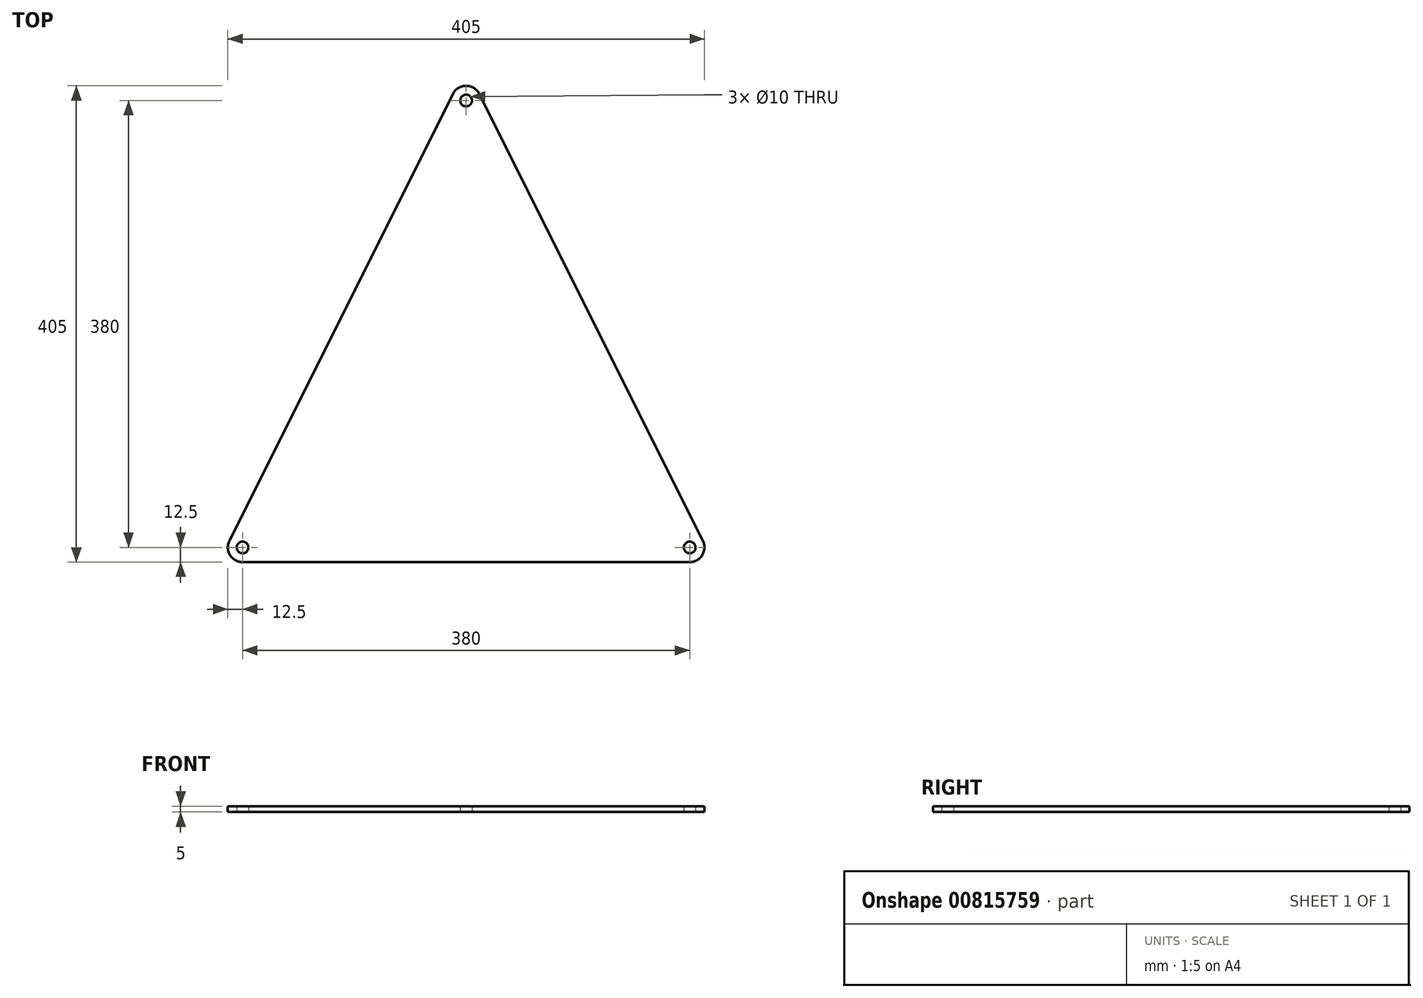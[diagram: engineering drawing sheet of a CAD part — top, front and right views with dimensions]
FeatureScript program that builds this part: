
annotation { "Feature Type Name" : "Feature", "Feature Type Description" : "" }
export const myFeature = defineFeature(function(context is Context, id is Id, definition is map)
    precondition{}
    {
        {
            var Q0;
            Q0=qCreatedBy(makeId("Top.planeOp"),FACE);
            var sketch = newSketch(context, id + "F0", { "sketchPlane" : qUnion([Q0])});
            skPoint(sketch, "E0", {"position": v(0, 190) * mm});
            skCircle(sketch, "E1", {"center": v(0, 190) * mm, "radius": 12.5 * mm});
            skPoint(sketch, "E2", {"position": v(0, -190) * mm});
            skLineSegment(sketch, "E3.top", {"start": v(190, -190) * mm, "end": v(-190, -190) * mm});
            skLineSegment(sketch, "E3.left", {"start": v(190, -190) * mm, "end": v(190, -190) * mm});
            skLineSegment(sketch, "E3.right", {"start": v(-190, -190) * mm, "end": v(-190, -190) * mm});
            skCircle(sketch, "E4", {"center": v(-190, -190) * mm, "radius": 12.5 * mm});
            skCircle(sketch, "E5", {"center": v(190, -190) * mm, "radius": 12.5 * mm});
            skLineSegment(sketch, "E6", {"start": v(0, 190) * mm, "end": v(190, -190) * mm});
            skLineSegment(sketch, "E7", {"start": v(0, 190) * mm, "end": v(-190, -190) * mm});
            skLineSegment(sketch, "E8", {"start": v(0, 190) * mm, "end": v(11.18, 184.4) * mm, "construction": true});
            skLineSegment(sketch, "E9", {"start": v(0, 190) * mm, "end": v(-11.18, 195.6) * mm, "construction": true});
            skLineSegment(sketch, "E10", {"start": v(0, 190) * mm, "end": v(-11.18, 184.4) * mm, "construction": true});
            skLineSegment(sketch, "E11", {"start": v(0, 190) * mm, "end": v(11.18, 195.6) * mm, "construction": true});
            skLineSegment(sketch, "E12", {"start": v(190, -190) * mm, "end": v(201.18, -184.4) * mm, "construction": true});
            skLineSegment(sketch, "E13", {"start": v(190, -190) * mm, "end": v(178.82, -195.6) * mm, "construction": true});
            skLineSegment(sketch, "E14", {"start": v(190, -190) * mm, "end": v(190, -202.5) * mm, "construction": true});
            skLineSegment(sketch, "E15", {"start": v(190, -190) * mm, "end": v(190, -177.5) * mm, "construction": true});
            skLineSegment(sketch, "E16", {"start": v(-190, -190) * mm, "end": v(-190, -202.5) * mm, "construction": true});
            skLineSegment(sketch, "E17", {"start": v(-190, -190) * mm, "end": v(-190, -177.5) * mm, "construction": true});
            skLineSegment(sketch, "E18", {"start": v(-190, -190) * mm, "end": v(-201.18, -184.4) * mm, "construction": true});
            skLineSegment(sketch, "E19", {"start": v(-190, -190) * mm, "end": v(-178.82, -195.6) * mm, "construction": true});
            skLineSegment(sketch, "E20", {"start": v(-11.18, 195.6) * mm, "end": v(-201.18, -184.4) * mm});
            skLineSegment(sketch, "E21", {"start": v(11.18, 195.6) * mm, "end": v(201.18, -184.4) * mm});
            skLineSegment(sketch, "E22", {"start": v(190, -202.5) * mm, "end": v(-190, -202.5) * mm});
            skLineSegment(sketch, "E23", {"start": v(-11.18, 184.4) * mm, "end": v(178.82, -195.6) * mm});
            skLineSegment(sketch, "E24", {"start": v(11.18, 184.4) * mm, "end": v(-178.82, -195.6) * mm});
            skLineSegment(sketch, "E25", {"start": v(-190, -177.5) * mm, "end": v(190, -177.5) * mm});
            skLineSegment(sketch, "E26", {"start": v(-201.18, -184.4) * mm, "end": v(-210.23, -202.5) * mm});
            skLineSegment(sketch, "E27", {"start": v(-210.23, -202.5) * mm, "end": v(-190, -202.5) * mm});
            skLineSegment(sketch, "E28", {"start": v(201.18, -184.4) * mm, "end": v(210.23, -202.5) * mm});
            skLineSegment(sketch, "E29", {"start": v(210.23, -202.5) * mm, "end": v(190, -202.5) * mm});
            skLineSegment(sketch, "E30", {"start": v(11.18, 195.6) * mm, "end": v(0, 217.95) * mm});
            skLineSegment(sketch, "E31", {"start": v(0, 217.95) * mm, "end": v(-11.18, 195.6) * mm});
            skCircle(sketch, "E32", {"center": v(0, 190) * mm, "radius": 5 * mm});
            skCircle(sketch, "E33", {"center": v(-190, -190) * mm, "radius": 5 * mm});
            skCircle(sketch, "E34", {"center": v(190, -190) * mm, "radius": 5 * mm});
            skSolve(sketch);
        }
        {
            var Q0;
            {var subQ0=sQuery(id+"F0.wireOp",EDGE,"E1");var subQ7=makeQuery(id+"F0.imprint","INTERSECT",VERTEX,{"derivedFrom":[subQ0,sQuery(id+"F0.wireOp",EDGE,"E20")]});Q0=makeQuery(id+"F0.imprint","IMPRINT",FACE,{"disambiguationData":[TD([[makeQuery(id+"F0.imprint","IMPRINT",EDGE,{"disambiguationData":[TD([[subQ7,1.0]])],"derivedFrom":subQ0}),1.0]])]});}
            var Q1;
            {var subQ5=sQuery(id+"F0.wireOp",EDGE,"E20");Q1=makeQuery(id+"F0.imprint","IMPRINT",FACE,{"disambiguationData":[TD([[makeQuery(id+"F0.imprint","IMPRINT",EDGE,{"derivedFrom":subQ5}),1.0]])]});}
            var Q2;
            {var subQ0=sQuery(id+"F0.wireOp",EDGE,"E21");Q2=makeQuery(id+"F0.imprint","IMPRINT",FACE,{"disambiguationData":[TD([[makeQuery(id+"F0.imprint","IMPRINT",EDGE,{"derivedFrom":subQ0}),-1.0]])]});}
            var Q3;
            {var subQ0=sQuery(id+"F0.wireOp",EDGE,"E22");Q3=makeQuery(id+"F0.imprint","IMPRINT",FACE,{"disambiguationData":[TD([[makeQuery(id+"F0.imprint","IMPRINT",EDGE,{"derivedFrom":subQ0}),-1.0]])]});}
            var Q4;
            {var subQ0=sQuery(id+"F0.wireOp",EDGE,"E24");var subQ1=sQuery(id+"F0.wireOp",EDGE,"E6");var subQ2=makeQuery(id+"F0.imprint","INTERSECT",VERTEX,{"derivedFrom":[subQ1,subQ0]});Q4=makeQuery(id+"F0.imprint","IMPRINT",FACE,{"disambiguationData":[TD([[makeQuery(id+"F0.imprint","IMPRINT",EDGE,{"disambiguationData":[TD([[subQ2,-1.0]])],"derivedFrom":subQ1}),-1.0]])]});}
            var Q5;
            {var subQ0=sQuery(id+"F0.wireOp",EDGE,"E7");var subQ1=sQuery(id+"F0.wireOp",EDGE,"E1");var subQ2=makeQuery(id+"F0.imprint","INTERSECT",VERTEX,{"derivedFrom":[subQ1,subQ0]});Q5=makeQuery(id+"F0.imprint","IMPRINT",FACE,{"disambiguationData":[TD([[makeQuery(id+"F0.imprint","IMPRINT",EDGE,{"disambiguationData":[TD([[subQ2,-1.0]])],"derivedFrom":subQ1}),1.0]])]});}
            var Q6;
            {var subQ0=sQuery(id+"F0.wireOp",EDGE,"E23");var subQ1=sQuery(id+"F0.wireOp",EDGE,"E3.top");var subQ2=makeQuery(id+"F0.imprint","INTERSECT",VERTEX,{"derivedFrom":[subQ1,subQ0]});Q6=makeQuery(id+"F0.imprint","IMPRINT",FACE,{"disambiguationData":[TD([[makeQuery(id+"F0.imprint","IMPRINT",EDGE,{"disambiguationData":[TD([[subQ2,-1.0]])],"derivedFrom":subQ1}),-1.0]])]});}
            var Q7;
            {var subQ0=sQuery(id+"F0.wireOp",EDGE,"E23");var subQ1=sQuery(id+"F0.wireOp",EDGE,"E7");var subQ2=makeQuery(id+"F0.imprint","INTERSECT",VERTEX,{"derivedFrom":[subQ1,subQ0]});Q7=makeQuery(id+"F0.imprint","IMPRINT",FACE,{"disambiguationData":[TD([[makeQuery(id+"F0.imprint","IMPRINT",EDGE,{"disambiguationData":[TD([[subQ2,-1.0]])],"derivedFrom":subQ1}),1.0]])]});}
            var Q8;
            {var subQ1=sQuery(id+"F0.wireOp",EDGE,"E7");var subQ5=sQuery(id+"F0.wireOp",EDGE,"E1");var subQ6=makeQuery(id+"F0.imprint","INTERSECT",VERTEX,{"derivedFrom":[subQ5,subQ1]});Q8=makeQuery(id+"F0.imprint","IMPRINT",FACE,{"disambiguationData":[TD([[makeQuery(id+"F0.imprint","IMPRINT",EDGE,{"disambiguationData":[TD([[subQ6,-1.0]])],"derivedFrom":subQ5}),-1.0]])]});}
            var Q9;
            {var subQ5=sQuery(id+"F0.wireOp",EDGE,"E24");var subQ6=sQuery(id+"F0.wireOp",EDGE,"E3.top");var subQ7=makeQuery(id+"F0.imprint","INTERSECT",VERTEX,{"derivedFrom":[subQ6,subQ5]});Q9=makeQuery(id+"F0.imprint","IMPRINT",FACE,{"disambiguationData":[TD([[makeQuery(id+"F0.imprint","IMPRINT",EDGE,{"disambiguationData":[TD([[subQ7,-1.0]])],"derivedFrom":subQ6}),-1.0]])]});}
            var Q10;
            {var subQ1=sQuery(id+"F0.wireOp",EDGE,"E5");var subQ6=sQuery(id+"F0.wireOp",EDGE,"E3.top");var subQ9=makeQuery(id+"F0.imprint","INTERSECT",VERTEX,{"derivedFrom":[subQ6,subQ1]});Q10=makeQuery(id+"F0.imprint","IMPRINT",FACE,{"disambiguationData":[TD([[makeQuery(id+"F0.imprint","IMPRINT",EDGE,{"disambiguationData":[TD([[subQ9,-1.0]])],"derivedFrom":subQ6}),-1.0]])]});}
            var Q11;
            {var subQ0=sQuery(id+"F0.wireOp",EDGE,"E24");var subQ1=sQuery(id+"F0.wireOp",EDGE,"E3.top");var subQ2=makeQuery(id+"F0.imprint","INTERSECT",VERTEX,{"derivedFrom":[subQ1,subQ0]});Q11=makeQuery(id+"F0.imprint","IMPRINT",FACE,{"disambiguationData":[TD([[makeQuery(id+"F0.imprint","IMPRINT",EDGE,{"disambiguationData":[TD([[subQ2,-1.0]])],"derivedFrom":subQ1}),1.0]])]});}
            var Q12;
            {var subQ0=sQuery(id+"F0.wireOp",EDGE,"E24");var subQ1=sQuery(id+"F0.wireOp",EDGE,"E1");var subQ2=makeQuery(id+"F0.imprint","INTERSECT",VERTEX,{"derivedFrom":[subQ1,subQ0]});Q12=makeQuery(id+"F0.imprint","IMPRINT",FACE,{"disambiguationData":[TD([[makeQuery(id+"F0.imprint","IMPRINT",EDGE,{"disambiguationData":[TD([[subQ2,1.0]])],"derivedFrom":subQ1}),-1.0]])]});}
            var Q13;
            {var subQ0=sQuery(id+"F0.wireOp",EDGE,"E23");var subQ1=sQuery(id+"F0.wireOp",EDGE,"E1");var subQ2=makeQuery(id+"F0.imprint","INTERSECT",VERTEX,{"derivedFrom":[subQ1,subQ0]});Q13=makeQuery(id+"F0.imprint","IMPRINT",FACE,{"disambiguationData":[TD([[makeQuery(id+"F0.imprint","IMPRINT",EDGE,{"disambiguationData":[TD([[subQ2,-1.0]])],"derivedFrom":subQ1}),-1.0]])]});}
            var Q14;
            {var subQ0=sQuery(id+"F0.wireOp",EDGE,"E5");var subQ1=sQuery(id+"F0.wireOp",EDGE,"E3.top");var subQ2=makeQuery(id+"F0.imprint","INTERSECT",VERTEX,{"derivedFrom":[subQ1,subQ0]});Q14=makeQuery(id+"F0.imprint","IMPRINT",FACE,{"disambiguationData":[TD([[makeQuery(id+"F0.imprint","IMPRINT",EDGE,{"disambiguationData":[TD([[subQ2,-1.0]])],"derivedFrom":subQ1}),1.0]])]});}
            var Q15;
            {var subQ0=sQuery(id+"F0.wireOp",EDGE,"E25");var subQ1=sQuery(id+"F0.wireOp",EDGE,"E5");var subQ2=makeQuery(id+"F0.imprint","INTERSECT",VERTEX,{"derivedFrom":[subQ1,subQ0]});Q15=makeQuery(id+"F0.imprint","IMPRINT",FACE,{"disambiguationData":[TD([[makeQuery(id+"F0.imprint","IMPRINT",EDGE,{"disambiguationData":[TD([[subQ2,-1.0]])],"derivedFrom":subQ1}),-1.0]])]});}
            var Q16;
            {var subQ0=sQuery(id+"F0.wireOp",EDGE,"E25");var subQ1=sQuery(id+"F0.wireOp",EDGE,"E4");var subQ2=makeQuery(id+"F0.imprint","INTERSECT",VERTEX,{"derivedFrom":[subQ1,subQ0]});Q16=makeQuery(id+"F0.imprint","IMPRINT",FACE,{"disambiguationData":[TD([[makeQuery(id+"F0.imprint","IMPRINT",EDGE,{"disambiguationData":[TD([[subQ2,1.0]])],"derivedFrom":subQ1}),-1.0]])]});}
            var Q17;
            {var subQ0=sQuery(id+"F0.wireOp",EDGE,"E4");var subQ8=sQuery(id+"F0.wireOp",EDGE,"E3.top");var subQ9=makeQuery(id+"F0.imprint","INTERSECT",VERTEX,{"derivedFrom":[subQ8,subQ0]});Q17=makeQuery(id+"F0.imprint","IMPRINT",FACE,{"disambiguationData":[TD([[makeQuery(id+"F0.imprint","IMPRINT",EDGE,{"disambiguationData":[TD([[subQ9,-1.0]])],"derivedFrom":subQ8}),1.0]])]});}
            var Q18;
            {var subQ0=sQuery(id+"F0.wireOp",EDGE,"E4");var subQ1=sQuery(id+"F0.wireOp",EDGE,"E3.top");var subQ2=makeQuery(id+"F0.imprint","INTERSECT",VERTEX,{"derivedFrom":[subQ1,subQ0]});Q18=makeQuery(id+"F0.imprint","IMPRINT",FACE,{"disambiguationData":[TD([[makeQuery(id+"F0.imprint","IMPRINT",EDGE,{"disambiguationData":[TD([[subQ2,-1.0]])],"derivedFrom":subQ1}),-1.0]])]});}
            var Q19;
            {var subQ5=sQuery(id+"F0.wireOp",EDGE,"E34");var subQ8=sQuery(id+"F0.wireOp",EDGE,"E3.top");var subQ10=makeQuery(id+"F0.imprint","INTERSECT",VERTEX,{"derivedFrom":[subQ8,subQ5]});Q19=makeQuery(id+"F0.imprint","IMPRINT",FACE,{"disambiguationData":[TD([[makeQuery(id+"F0.imprint","IMPRINT",EDGE,{"disambiguationData":[TD([[subQ10,-1.0]])],"derivedFrom":subQ8}),1.0]])]});}
            var Q20;
            {var subQ0=sQuery(id+"F0.wireOp",EDGE,"E34");var subQ1=sQuery(id+"F0.wireOp",EDGE,"E3.top");var subQ2=makeQuery(id+"F0.imprint","INTERSECT",VERTEX,{"derivedFrom":[subQ1,subQ0]});Q20=makeQuery(id+"F0.imprint","IMPRINT",FACE,{"disambiguationData":[TD([[makeQuery(id+"F0.imprint","IMPRINT",EDGE,{"disambiguationData":[TD([[subQ2,-1.0]])],"derivedFrom":subQ1}),-1.0]])]});}
            var Q21;
            {var subQ0=sQuery(id+"F0.wireOp",EDGE,"E24");var subQ1=sQuery(id+"F0.wireOp",EDGE,"E23");var subQ2=makeQuery(id+"F0.imprint","INTERSECT",VERTEX,{"derivedFrom":[subQ1,subQ0]});Q21=makeQuery(id+"F0.imprint","IMPRINT",FACE,{"disambiguationData":[TD([[makeQuery(id+"F0.imprint","IMPRINT",EDGE,{"disambiguationData":[TD([[subQ2,-1.0]])],"derivedFrom":subQ1}),-1.0]])]});}
            extrude(context, id + "F1", {"entities" : qUnion([Q0, Q1, Q2, Q3, Q4, Q5, Q6, Q7, Q8, Q9, Q10, Q11, Q12, Q13, Q14, Q15, Q16, Q17, Q18, Q19, Q20, Q21]), "depth" : 5 * mm, "offsetDistance" : 25 * mm});
        }
    });
